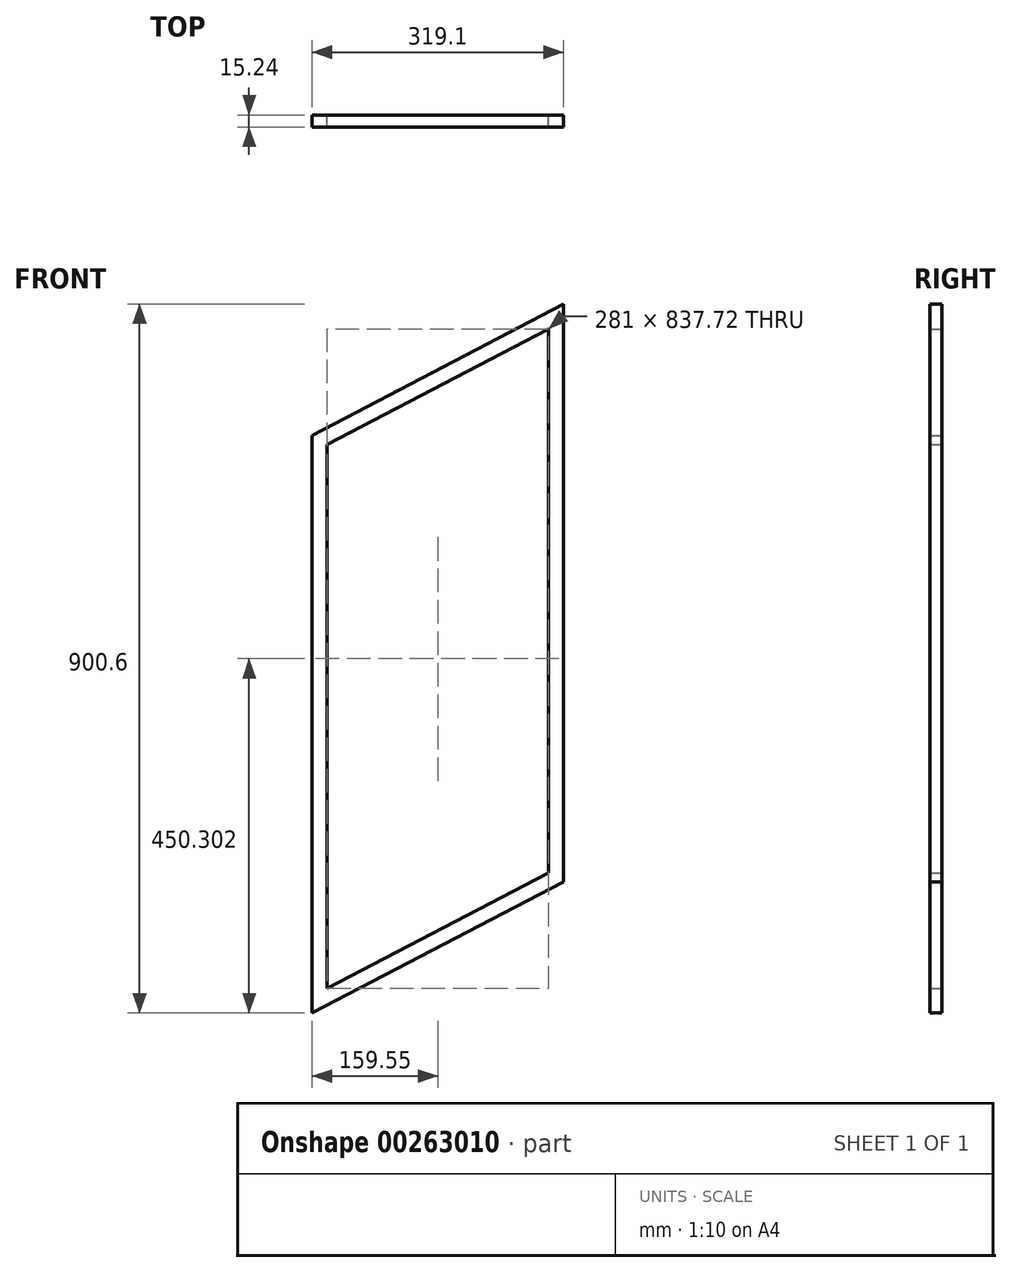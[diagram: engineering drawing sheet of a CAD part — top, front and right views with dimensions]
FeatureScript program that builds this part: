
annotation { "Feature Type Name" : "Feature", "Feature Type Description" : "" }
export const myFeature = defineFeature(function(context is Context, id is Id, definition is map)
    precondition{}
    {
        {
            var Q0;
            Q0=qCreatedBy(makeId("Front.planeOp"),FACE);
            var sketch = newSketch(context, id + "F0", { "sketchPlane" : qUnion([Q0])});
            skLineSegment(sketch, "E0", {"start": v(0, 0) * mm, "end": v(281, 146.72) * mm});
            skLineSegment(sketch, "E1", {"start": v(281, 146.72) * mm, "end": v(281, 837.72) * mm});
            skLineSegment(sketch, "E2", {"start": v(281, 837.72) * mm, "end": v(0, 691) * mm});
            skLineSegment(sketch, "E3", {"start": v(0, 691) * mm, "end": v(0, 0) * mm});
            skLineSegment(sketch, "E4.0", {"start": v(-19.05, 702.54) * mm, "end": v(-19.05, -31.44) * mm});
            skLineSegment(sketch, "E4.1", {"start": v(300.05, 869.16) * mm, "end": v(-19.05, 702.54) * mm});
            skLineSegment(sketch, "E4.2", {"start": v(300.05, 135.18) * mm, "end": v(300.05, 869.16) * mm});
            skLineSegment(sketch, "E4.3", {"start": v(-19.05, -31.44) * mm, "end": v(300.05, 135.18) * mm});
            skSolve(sketch);
        }
        {
            var Q0;
            Q0 = qSketchRegion(id + "F0", true);
            extrude(context, id + "F1", {"entities" : qUnion([Q0]), "depth" : 15.24 * mm});
        }
    });
